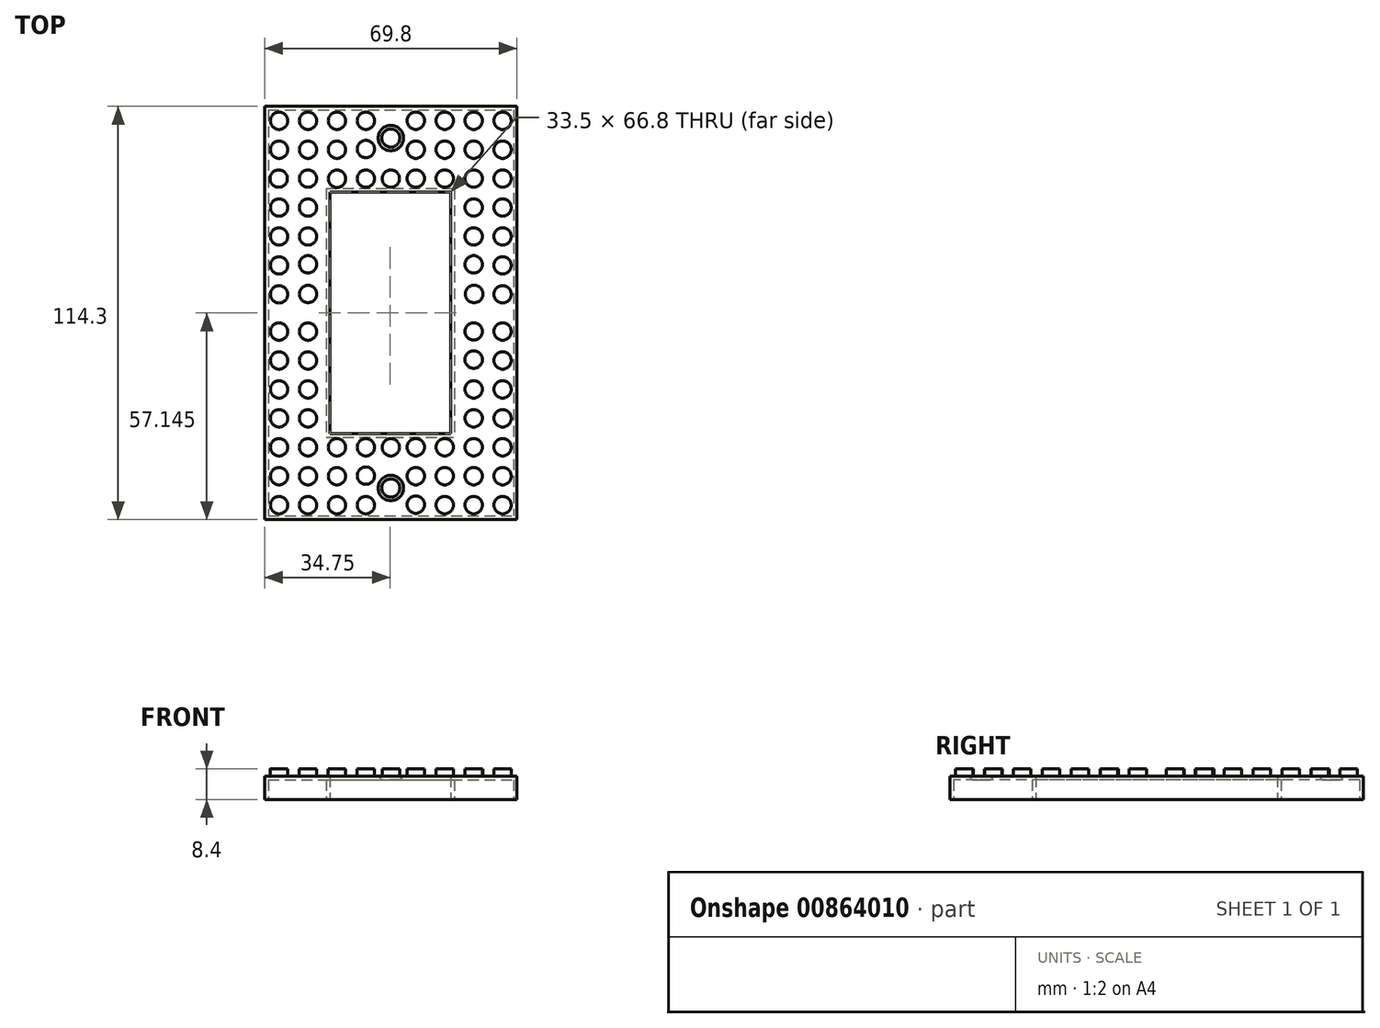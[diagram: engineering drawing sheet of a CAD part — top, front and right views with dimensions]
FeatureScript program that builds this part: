
annotation { "Feature Type Name" : "Feature", "Feature Type Description" : "" }
export const myFeature = defineFeature(function(context is Context, id is Id, definition is map)
    precondition{}
    {
        {
            var Q0;
            Q0=qCreatedBy(makeId("Top.planeOp"),FACE);
            var sketch = newSketch(context, id + "F0", { "sketchPlane" : qUnion([Q0])});
            skLineSegment(sketch, "E0.bottom", {"start": v(-34.9, 65.9) * mm, "end": v(34.9, 65.9) * mm});
            skLineSegment(sketch, "E0.top", {"start": v(-34.9, -48.4) * mm, "end": v(34.9, -48.4) * mm});
            skLineSegment(sketch, "E0.left", {"start": v(-34.9, 65.9) * mm, "end": v(-34.9, -48.4) * mm});
            skLineSegment(sketch, "E0.right", {"start": v(34.9, 65.9) * mm, "end": v(34.9, -48.4) * mm});
            skLineSegment(sketch, "E1.bottom", {"start": v(-16.9, 42.15) * mm, "end": v(16.6, 42.15) * mm});
            skLineSegment(sketch, "E1.top", {"start": v(-16.9, -24.65) * mm, "end": v(16.6, -24.65) * mm});
            skLineSegment(sketch, "E1.left", {"start": v(-16.9, 42.15) * mm, "end": v(-16.9, -24.65) * mm});
            skLineSegment(sketch, "E1.right", {"start": v(16.6, 42.15) * mm, "end": v(16.6, -24.65) * mm});
            skPoint(sketch, "E2", {"position": v(0, 57.15) * mm});
            skPoint(sketch, "E3", {"position": v(0, -39.65) * mm});
            skSolve(sketch);
        }
        {
            var Q0;
            Q0=makeQuery(id+"F0.imprint","IMPRINT",FACE,{"disambiguationData":[TD([[makeQuery(id+"F0.imprint","IMPRINT",EDGE,{"derivedFrom":sQuery(id+"F0.wireOp",EDGE,"E0.bottom")}),-1.0]])]});
            extrude(context, id + "F1", {"entities" : qUnion([Q0]), "depth" : 6.4 * mm, "offsetDistance" : 25 * mm});
        }
        {
            var Q0;
            Q0=makeQuery(id+"F1.opExtrude","CAP_FACE",FACE,{"disambiguationData":[OSD([sQuery(id+"F0.wireOp",EDGE,"E0.bottom"),sQuery(id+"F0.wireOp",EDGE,"E0.top"),sQuery(id+"F0.wireOp",EDGE,"E0.left"),sQuery(id+"F0.wireOp",EDGE,"E0.right"),sQuery(id+"F0.wireOp",EDGE,"E1.bottom"),sQuery(id+"F0.wireOp",EDGE,"E1.top"),sQuery(id+"F0.wireOp",EDGE,"E1.left"),sQuery(id+"F0.wireOp",EDGE,"E1.right"),sQuery(id+"F0.wireOp",EDGE,"O5FTPcTM-QUJB-rhsi-xSIB-Mxk94AfWPKoa"),sQuery(id+"F0.wireOp",EDGE,"3cRLo2FR-j5J2-G38M-Sb06-RW8L4j5h2IR9")])],"isStart":true});
            shell(context, id + "F2", {"entities" : qUnion([Q0]), "thickness" : 1 * mm});
        }
        {
            var Q0;
            Q0=makeQuery(id+"F1.opExtrude","CAP_FACE",FACE,{"disambiguationData":[OSD([sQuery(id+"F0.wireOp",EDGE,"E0.bottom"),sQuery(id+"F0.wireOp",EDGE,"E0.top"),sQuery(id+"F0.wireOp",EDGE,"E0.left"),sQuery(id+"F0.wireOp",EDGE,"E0.right"),sQuery(id+"F0.wireOp",EDGE,"E1.bottom"),sQuery(id+"F0.wireOp",EDGE,"E1.top"),sQuery(id+"F0.wireOp",EDGE,"E1.left"),sQuery(id+"F0.wireOp",EDGE,"E1.right"),sQuery(id+"F0.wireOp",EDGE,"O5FTPcTM-QUJB-rhsi-xSIB-Mxk94AfWPKoa"),sQuery(id+"F0.wireOp",EDGE,"3cRLo2FR-j5J2-G38M-Sb06-RW8L4j5h2IR9")])],"isStart":false});
            var sketch = newSketch(context, id + "F3", { "sketchPlane" : qUnion([Q0])});
            skLineSegment(sketch, "E4", {"start": v(-34.9, 65.9) * mm, "end": v(34.9, 65.9) * mm});
            skLineSegment(sketch, "E5", {"start": v(34.9, 65.9) * mm, "end": v(34.9, -48.4) * mm});
            skLineSegment(sketch, "E6", {"start": v(34.9, -48.4) * mm, "end": v(-34.9, -48.4) * mm});
            skLineSegment(sketch, "E7", {"start": v(-34.9, -48.4) * mm, "end": v(-34.9, 65.9) * mm});
            skCircle(sketch, "E8", {"center": v(-30.9, 61.9) * mm, "radius": 2.4 * mm});
            skCircle(sketch, "E9", {"center": v(-30.9, 53.9) * mm, "radius": 2.4 * mm});
            skCircle(sketch, "E10", {"center": v(-31, 45.9) * mm, "radius": 2.4 * mm});
            skCircle(sketch, "E11", {"center": v(-30.9, 37.9) * mm, "radius": 2.4 * mm});
            skCircle(sketch, "E12", {"center": v(-30.9, 29.9) * mm, "radius": 2.4 * mm});
            skCircle(sketch, "E13", {"center": v(-30.9, 21.9) * mm, "radius": 2.4 * mm});
            skCircle(sketch, "E14", {"center": v(-30.9, 13.9) * mm, "radius": 2.4 * mm});
            skCircle(sketch, "E15", {"center": v(-30.9, 3.6) * mm, "radius": 2.4 * mm});
            skCircle(sketch, "E16", {"center": v(-30.9, -4.4) * mm, "radius": 2.4 * mm});
            skCircle(sketch, "E17", {"center": v(-30.9, -12.4) * mm, "radius": 2.4 * mm});
            skCircle(sketch, "E18", {"center": v(-30.9, -20.4) * mm, "radius": 2.4 * mm});
            skCircle(sketch, "E19", {"center": v(-30.9, -28.4) * mm, "radius": 2.4 * mm});
            skCircle(sketch, "E20", {"center": v(-30.9, -36.4) * mm, "radius": 2.4 * mm});
            skCircle(sketch, "E21", {"center": v(-30.9, -44.4) * mm, "radius": 2.4 * mm});
            skCircle(sketch, "E22", {"center": v(-22.9, 61.9) * mm, "radius": 2.4 * mm});
            skCircle(sketch, "E23", {"center": v(-22.9, 53.9) * mm, "radius": 2.4 * mm});
            skCircle(sketch, "E24", {"center": v(-22.9, 37.9) * mm, "radius": 2.4 * mm});
            skCircle(sketch, "E25", {"center": v(-22.9, 29.9) * mm, "radius": 2.4 * mm});
            skCircle(sketch, "E26", {"center": v(-22.9, 22.22) * mm, "radius": 2.4 * mm});
            skCircle(sketch, "E27", {"center": v(-22.9, 13.98) * mm, "radius": 2.4 * mm});
            skCircle(sketch, "E28", {"center": v(-22.9, 3.6) * mm, "radius": 2.4 * mm});
            skCircle(sketch, "E29", {"center": v(-22.9, -4.4) * mm, "radius": 2.4 * mm});
            skCircle(sketch, "E30", {"center": v(-22.9, -12.4) * mm, "radius": 2.4 * mm});
            skCircle(sketch, "E31", {"center": v(-22.9, -20.4) * mm, "radius": 2.4 * mm});
            skCircle(sketch, "E32", {"center": v(-22.9, -28.4) * mm, "radius": 2.4 * mm});
            skCircle(sketch, "E33", {"center": v(-22.9, -36.4) * mm, "radius": 2.4 * mm});
            skCircle(sketch, "E34", {"center": v(-22.9, -44.4) * mm, "radius": 2.4 * mm});
            skCircle(sketch, "E35", {"center": v(-14.9, 61.9) * mm, "radius": 2.4 * mm});
            skCircle(sketch, "E36", {"center": v(-14.9, 53.9) * mm, "radius": 2.4 * mm});
            skCircle(sketch, "E37", {"center": v(-14.9, 45.86) * mm, "radius": 2.4 * mm});
            skCircle(sketch, "E38", {"center": v(-6.9, 61.9) * mm, "radius": 2.4 * mm});
            skCircle(sketch, "E39", {"center": v(-6.9, 54.09) * mm, "radius": 2.4 * mm});
            skCircle(sketch, "E40", {"center": v(-6.9, 45.9) * mm, "radius": 2.4 * mm});
            skCircle(sketch, "E41", {"center": v(-14.9, -28.4) * mm, "radius": 2.4 * mm});
            skCircle(sketch, "E42", {"center": v(-14.9, -36.4) * mm, "radius": 2.4 * mm});
            skCircle(sketch, "E43", {"center": v(-14.9, -44.4) * mm, "radius": 2.4 * mm});
            skCircle(sketch, "E44", {"center": v(0, 45.9) * mm, "radius": 2.4 * mm});
            skCircle(sketch, "E45", {"center": v(6.9, 61.9) * mm, "radius": 2.4 * mm});
            skCircle(sketch, "E46", {"center": v(6.9, 53.88) * mm, "radius": 2.4 * mm});
            skCircle(sketch, "E47", {"center": v(6.9, 45.9) * mm, "radius": 2.4 * mm});
            skCircle(sketch, "E48", {"center": v(14.9, 61.9) * mm, "radius": 2.4 * mm});
            skCircle(sketch, "E49", {"center": v(14.9, 53.9) * mm, "radius": 2.4 * mm});
            skCircle(sketch, "E50", {"center": v(14.9, 45.9) * mm, "radius": 2.4 * mm});
            skCircle(sketch, "E51", {"center": v(-6.9, -28.4) * mm, "radius": 2.4 * mm});
            skCircle(sketch, "E52", {"center": v(-6.9, -36.25) * mm, "radius": 2.4 * mm});
            skCircle(sketch, "E53", {"center": v(-6.9, -44.4) * mm, "radius": 2.4 * mm});
            skCircle(sketch, "E54", {"center": v(0, -28.4) * mm, "radius": 2.4 * mm});
            skCircle(sketch, "E55", {"center": v(6.9, -28.4) * mm, "radius": 2.4 * mm});
            skCircle(sketch, "E56", {"center": v(6.9, -36.4) * mm, "radius": 2.4 * mm});
            skCircle(sketch, "E57", {"center": v(6.9, -44.28) * mm, "radius": 2.4 * mm});
            skCircle(sketch, "E58", {"center": v(14.9, -28.4) * mm, "radius": 2.4 * mm});
            skCircle(sketch, "E59", {"center": v(14.9, -36.4) * mm, "radius": 2.4 * mm});
            skCircle(sketch, "E60", {"center": v(14.9, -44.4) * mm, "radius": 2.4 * mm});
            skCircle(sketch, "E61", {"center": v(22.9, 61.9) * mm, "radius": 2.4 * mm});
            skCircle(sketch, "E62", {"center": v(22.9, 53.9) * mm, "radius": 2.4 * mm});
            skCircle(sketch, "E63", {"center": v(22.9, 37.9) * mm, "radius": 2.4 * mm});
            skCircle(sketch, "E64", {"center": v(22.9, 29.9) * mm, "radius": 2.4 * mm});
            skCircle(sketch, "E65", {"center": v(22.9, 22.22) * mm, "radius": 2.4 * mm});
            skCircle(sketch, "E66", {"center": v(23.03, 13.98) * mm, "radius": 2.4 * mm});
            skCircle(sketch, "E67", {"center": v(22.9, 3.64) * mm, "radius": 2.4 * mm});
            skCircle(sketch, "E68", {"center": v(22.9, -4.17) * mm, "radius": 2.4 * mm});
            skCircle(sketch, "E69", {"center": v(22.9, -12.4) * mm, "radius": 2.4 * mm});
            skCircle(sketch, "E70", {"center": v(22.9, -20.4) * mm, "radius": 2.4 * mm});
            skCircle(sketch, "E71", {"center": v(22.9, -28.4) * mm, "radius": 2.4 * mm});
            skCircle(sketch, "E72", {"center": v(22.9, -36.4) * mm, "radius": 2.4 * mm});
            skCircle(sketch, "E73", {"center": v(22.9, -44.4) * mm, "radius": 2.4 * mm});
            skCircle(sketch, "E74", {"center": v(30.9, -44.4) * mm, "radius": 2.4 * mm});
            skCircle(sketch, "E75", {"center": v(30.9, -36.4) * mm, "radius": 2.4 * mm});
            skCircle(sketch, "E76", {"center": v(30.9, -28.4) * mm, "radius": 2.4 * mm});
            skCircle(sketch, "E77", {"center": v(30.9, -20.4) * mm, "radius": 2.4 * mm});
            skCircle(sketch, "E78", {"center": v(30.9, -12.4) * mm, "radius": 2.4 * mm});
            skCircle(sketch, "E79", {"center": v(30.9, -4.4) * mm, "radius": 2.4 * mm});
            skCircle(sketch, "E80", {"center": v(30.9, 3.6) * mm, "radius": 2.4 * mm});
            skCircle(sketch, "E81", {"center": v(30.9, 13.9) * mm, "radius": 2.4 * mm});
            skCircle(sketch, "E82", {"center": v(30.9, 21.9) * mm, "radius": 2.4 * mm});
            skCircle(sketch, "E83", {"center": v(30.9, 29.9) * mm, "radius": 2.4 * mm});
            skCircle(sketch, "E84", {"center": v(30.9, 37.9) * mm, "radius": 2.4 * mm});
            skCircle(sketch, "E85", {"center": v(30.9, 45.9) * mm, "radius": 2.4 * mm});
            skCircle(sketch, "E86", {"center": v(30.9, 53.9) * mm, "radius": 2.4 * mm});
            skCircle(sketch, "E87", {"center": v(30.9, 61.9) * mm, "radius": 2.4 * mm});
            skCircle(sketch, "E88", {"center": v(-22.9, 45.9) * mm, "radius": 2.4 * mm});
            skCircle(sketch, "E89", {"center": v(22.9, 45.9) * mm, "radius": 2.4 * mm});
            skPoint(sketch, "E90", {"position": v(0, 57.12) * mm});
            skPoint(sketch, "E90.positionSnap0", {"position": v(0, 65.9) * mm});
            skPoint(sketch, "E91", {"position": v(0, -39.67) * mm});
            skSolve(sketch);
        }
        {
            var Q0;
            Q0=makeQuery(id+"F3.imprint","IMPRINT",FACE,{"disambiguationData":[TD([[makeQuery(id+"F3.imprint","IMPRINT",EDGE,{"derivedFrom":sQuery(id+"F3.wireOp",EDGE,"E74")}),1.0]])]});
            var Q1;
            Q1=makeQuery(id+"F3.imprint","IMPRINT",FACE,{"disambiguationData":[TD([[makeQuery(id+"F3.imprint","IMPRINT",EDGE,{"derivedFrom":sQuery(id+"F3.wireOp",EDGE,"E73")}),1.0]])]});
            var Q2;
            Q2=makeQuery(id+"F3.imprint","IMPRINT",FACE,{"disambiguationData":[TD([[makeQuery(id+"F3.imprint","IMPRINT",EDGE,{"derivedFrom":sQuery(id+"F3.wireOp",EDGE,"E60")}),1.0]])]});
            var Q3;
            Q3=makeQuery(id+"F3.imprint","IMPRINT",FACE,{"disambiguationData":[TD([[makeQuery(id+"F3.imprint","IMPRINT",EDGE,{"derivedFrom":sQuery(id+"F3.wireOp",EDGE,"E57")}),1.0]])]});
            var Q4;
            Q4=makeQuery(id+"F3.imprint","IMPRINT",FACE,{"disambiguationData":[TD([[makeQuery(id+"F3.imprint","IMPRINT",EDGE,{"derivedFrom":sQuery(id+"F3.wireOp",EDGE,"E53")}),1.0]])]});
            var Q5;
            Q5=makeQuery(id+"F3.imprint","IMPRINT",FACE,{"disambiguationData":[TD([[makeQuery(id+"F3.imprint","IMPRINT",EDGE,{"derivedFrom":sQuery(id+"F3.wireOp",EDGE,"E43")}),1.0]])]});
            var Q6;
            Q6=makeQuery(id+"F3.imprint","IMPRINT",FACE,{"disambiguationData":[TD([[makeQuery(id+"F3.imprint","IMPRINT",EDGE,{"derivedFrom":sQuery(id+"F3.wireOp",EDGE,"E34")}),1.0]])]});
            var Q7;
            Q7=makeQuery(id+"F3.imprint","IMPRINT",FACE,{"disambiguationData":[TD([[makeQuery(id+"F3.imprint","IMPRINT",EDGE,{"derivedFrom":sQuery(id+"F3.wireOp",EDGE,"E21")}),1.0]])]});
            var Q8;
            Q8=makeQuery(id+"F3.imprint","IMPRINT",FACE,{"disambiguationData":[TD([[makeQuery(id+"F3.imprint","IMPRINT",EDGE,{"derivedFrom":sQuery(id+"F3.wireOp",EDGE,"E20")}),1.0]])]});
            var Q9;
            Q9=makeQuery(id+"F3.imprint","IMPRINT",FACE,{"disambiguationData":[TD([[makeQuery(id+"F3.imprint","IMPRINT",EDGE,{"derivedFrom":sQuery(id+"F3.wireOp",EDGE,"E33")}),1.0]])]});
            var Q10;
            Q10=makeQuery(id+"F3.imprint","IMPRINT",FACE,{"disambiguationData":[TD([[makeQuery(id+"F3.imprint","IMPRINT",EDGE,{"derivedFrom":sQuery(id+"F3.wireOp",EDGE,"E42")}),1.0]])]});
            var Q11;
            Q11=makeQuery(id+"F3.imprint","IMPRINT",FACE,{"disambiguationData":[TD([[makeQuery(id+"F3.imprint","IMPRINT",EDGE,{"derivedFrom":sQuery(id+"F3.wireOp",EDGE,"E52")}),1.0]])]});
            var Q12;
            Q12=makeQuery(id+"F3.imprint","IMPRINT",FACE,{"disambiguationData":[TD([[makeQuery(id+"F3.imprint","IMPRINT",EDGE,{"derivedFrom":sQuery(id+"F3.wireOp",EDGE,"E56")}),1.0]])]});
            var Q13;
            Q13=makeQuery(id+"F3.imprint","IMPRINT",FACE,{"disambiguationData":[TD([[makeQuery(id+"F3.imprint","IMPRINT",EDGE,{"derivedFrom":sQuery(id+"F3.wireOp",EDGE,"E59")}),1.0]])]});
            var Q14;
            Q14=makeQuery(id+"F3.imprint","IMPRINT",FACE,{"disambiguationData":[TD([[makeQuery(id+"F3.imprint","IMPRINT",EDGE,{"derivedFrom":sQuery(id+"F3.wireOp",EDGE,"E72")}),1.0]])]});
            var Q15;
            Q15=makeQuery(id+"F3.imprint","IMPRINT",FACE,{"disambiguationData":[TD([[makeQuery(id+"F3.imprint","IMPRINT",EDGE,{"derivedFrom":sQuery(id+"F3.wireOp",EDGE,"E75")}),1.0]])]});
            var Q16;
            Q16=makeQuery(id+"F3.imprint","IMPRINT",FACE,{"disambiguationData":[TD([[makeQuery(id+"F3.imprint","IMPRINT",EDGE,{"derivedFrom":sQuery(id+"F3.wireOp",EDGE,"E76")}),1.0]])]});
            var Q17;
            Q17=makeQuery(id+"F3.imprint","IMPRINT",FACE,{"disambiguationData":[TD([[makeQuery(id+"F3.imprint","IMPRINT",EDGE,{"derivedFrom":sQuery(id+"F3.wireOp",EDGE,"E71")}),1.0]])]});
            var Q18;
            Q18=makeQuery(id+"F3.imprint","IMPRINT",FACE,{"disambiguationData":[TD([[makeQuery(id+"F3.imprint","IMPRINT",EDGE,{"derivedFrom":sQuery(id+"F3.wireOp",EDGE,"E58")}),1.0]])]});
            var Q19;
            Q19=makeQuery(id+"F3.imprint","IMPRINT",FACE,{"disambiguationData":[TD([[makeQuery(id+"F3.imprint","IMPRINT",EDGE,{"derivedFrom":sQuery(id+"F3.wireOp",EDGE,"E55")}),1.0]])]});
            var Q20;
            Q20=makeQuery(id+"F3.imprint","IMPRINT",FACE,{"disambiguationData":[TD([[makeQuery(id+"F3.imprint","IMPRINT",EDGE,{"derivedFrom":sQuery(id+"F3.wireOp",EDGE,"E54")}),1.0]])]});
            var Q21;
            Q21=makeQuery(id+"F3.imprint","IMPRINT",FACE,{"disambiguationData":[TD([[makeQuery(id+"F3.imprint","IMPRINT",EDGE,{"derivedFrom":sQuery(id+"F3.wireOp",EDGE,"E51")}),1.0]])]});
            var Q22;
            Q22=makeQuery(id+"F3.imprint","IMPRINT",FACE,{"disambiguationData":[TD([[makeQuery(id+"F3.imprint","IMPRINT",EDGE,{"derivedFrom":sQuery(id+"F3.wireOp",EDGE,"E41")}),1.0]])]});
            var Q23;
            Q23=makeQuery(id+"F3.imprint","IMPRINT",FACE,{"disambiguationData":[TD([[makeQuery(id+"F3.imprint","IMPRINT",EDGE,{"derivedFrom":sQuery(id+"F3.wireOp",EDGE,"E32")}),1.0]])]});
            var Q24;
            Q24=makeQuery(id+"F3.imprint","IMPRINT",FACE,{"disambiguationData":[TD([[makeQuery(id+"F3.imprint","IMPRINT",EDGE,{"derivedFrom":sQuery(id+"F3.wireOp",EDGE,"E19")}),1.0]])]});
            var Q25;
            Q25=makeQuery(id+"F3.imprint","IMPRINT",FACE,{"disambiguationData":[TD([[makeQuery(id+"F3.imprint","IMPRINT",EDGE,{"derivedFrom":sQuery(id+"F3.wireOp",EDGE,"E18")}),1.0]])]});
            var Q26;
            Q26=makeQuery(id+"F3.imprint","IMPRINT",FACE,{"disambiguationData":[TD([[makeQuery(id+"F3.imprint","IMPRINT",EDGE,{"derivedFrom":sQuery(id+"F3.wireOp",EDGE,"E31")}),1.0]])]});
            var Q27;
            Q27=makeQuery(id+"F3.imprint","IMPRINT",FACE,{"disambiguationData":[TD([[makeQuery(id+"F3.imprint","IMPRINT",EDGE,{"derivedFrom":sQuery(id+"F3.wireOp",EDGE,"E70")}),1.0]])]});
            var Q28;
            Q28=makeQuery(id+"F3.imprint","IMPRINT",FACE,{"disambiguationData":[TD([[makeQuery(id+"F3.imprint","IMPRINT",EDGE,{"derivedFrom":sQuery(id+"F3.wireOp",EDGE,"E77")}),1.0]])]});
            var Q29;
            Q29=makeQuery(id+"F3.imprint","IMPRINT",FACE,{"disambiguationData":[TD([[makeQuery(id+"F3.imprint","IMPRINT",EDGE,{"derivedFrom":sQuery(id+"F3.wireOp",EDGE,"E17")}),1.0]])]});
            var Q30;
            Q30=makeQuery(id+"F3.imprint","IMPRINT",FACE,{"disambiguationData":[TD([[makeQuery(id+"F3.imprint","IMPRINT",EDGE,{"derivedFrom":sQuery(id+"F3.wireOp",EDGE,"E16")}),1.0]])]});
            var Q31;
            Q31=makeQuery(id+"F3.imprint","IMPRINT",FACE,{"disambiguationData":[TD([[makeQuery(id+"F3.imprint","IMPRINT",EDGE,{"derivedFrom":sQuery(id+"F3.wireOp",EDGE,"E15")}),1.0]])]});
            var Q32;
            Q32=makeQuery(id+"F3.imprint","IMPRINT",FACE,{"disambiguationData":[TD([[makeQuery(id+"F3.imprint","IMPRINT",EDGE,{"derivedFrom":sQuery(id+"F3.wireOp",EDGE,"E14")}),1.0]])]});
            var Q33;
            Q33=makeQuery(id+"F3.imprint","IMPRINT",FACE,{"disambiguationData":[TD([[makeQuery(id+"F3.imprint","IMPRINT",EDGE,{"derivedFrom":sQuery(id+"F3.wireOp",EDGE,"E12")}),1.0]])]});
            var Q34;
            Q34=makeQuery(id+"F3.imprint","IMPRINT",FACE,{"disambiguationData":[TD([[makeQuery(id+"F3.imprint","IMPRINT",EDGE,{"derivedFrom":sQuery(id+"F3.wireOp",EDGE,"E13")}),1.0]])]});
            var Q35;
            Q35=makeQuery(id+"F3.imprint","IMPRINT",FACE,{"disambiguationData":[TD([[makeQuery(id+"F3.imprint","IMPRINT",EDGE,{"derivedFrom":sQuery(id+"F3.wireOp",EDGE,"E11")}),1.0]])]});
            var Q36;
            Q36=makeQuery(id+"F3.imprint","IMPRINT",FACE,{"disambiguationData":[TD([[makeQuery(id+"F3.imprint","IMPRINT",EDGE,{"derivedFrom":sQuery(id+"F3.wireOp",EDGE,"E24")}),1.0]])]});
            var Q37;
            Q37=makeQuery(id+"F3.imprint","IMPRINT",FACE,{"disambiguationData":[TD([[makeQuery(id+"F3.imprint","IMPRINT",EDGE,{"derivedFrom":sQuery(id+"F3.wireOp",EDGE,"E25")}),1.0]])]});
            var Q38;
            Q38=makeQuery(id+"F3.imprint","IMPRINT",FACE,{"disambiguationData":[TD([[makeQuery(id+"F3.imprint","IMPRINT",EDGE,{"derivedFrom":sQuery(id+"F3.wireOp",EDGE,"E26")}),1.0]])]});
            var Q39;
            Q39=makeQuery(id+"F3.imprint","IMPRINT",FACE,{"disambiguationData":[TD([[makeQuery(id+"F3.imprint","IMPRINT",EDGE,{"derivedFrom":sQuery(id+"F3.wireOp",EDGE,"E27")}),1.0]])]});
            var Q40;
            Q40=makeQuery(id+"F3.imprint","IMPRINT",FACE,{"disambiguationData":[TD([[makeQuery(id+"F3.imprint","IMPRINT",EDGE,{"derivedFrom":sQuery(id+"F3.wireOp",EDGE,"E28")}),1.0]])]});
            var Q41;
            Q41=makeQuery(id+"F3.imprint","IMPRINT",FACE,{"disambiguationData":[TD([[makeQuery(id+"F3.imprint","IMPRINT",EDGE,{"derivedFrom":sQuery(id+"F3.wireOp",EDGE,"E29")}),1.0]])]});
            var Q42;
            Q42=makeQuery(id+"F3.imprint","IMPRINT",FACE,{"disambiguationData":[TD([[makeQuery(id+"F3.imprint","IMPRINT",EDGE,{"derivedFrom":sQuery(id+"F3.wireOp",EDGE,"E30")}),1.0]])]});
            var Q43;
            Q43=makeQuery(id+"F3.imprint","IMPRINT",FACE,{"disambiguationData":[TD([[makeQuery(id+"F3.imprint","IMPRINT",EDGE,{"derivedFrom":sQuery(id+"F3.wireOp",EDGE,"E69")}),1.0]])]});
            var Q44;
            Q44=makeQuery(id+"F3.imprint","IMPRINT",FACE,{"disambiguationData":[TD([[makeQuery(id+"F3.imprint","IMPRINT",EDGE,{"derivedFrom":sQuery(id+"F3.wireOp",EDGE,"E68")}),1.0]])]});
            var Q45;
            Q45=makeQuery(id+"F3.imprint","IMPRINT",FACE,{"disambiguationData":[TD([[makeQuery(id+"F3.imprint","IMPRINT",EDGE,{"derivedFrom":sQuery(id+"F3.wireOp",EDGE,"E67")}),1.0]])]});
            var Q46;
            Q46=makeQuery(id+"F3.imprint","IMPRINT",FACE,{"disambiguationData":[TD([[makeQuery(id+"F3.imprint","IMPRINT",EDGE,{"derivedFrom":sQuery(id+"F3.wireOp",EDGE,"E66")}),1.0]])]});
            var Q47;
            Q47=makeQuery(id+"F3.imprint","IMPRINT",FACE,{"disambiguationData":[TD([[makeQuery(id+"F3.imprint","IMPRINT",EDGE,{"derivedFrom":sQuery(id+"F3.wireOp",EDGE,"E65")}),1.0]])]});
            var Q48;
            Q48=makeQuery(id+"F3.imprint","IMPRINT",FACE,{"disambiguationData":[TD([[makeQuery(id+"F3.imprint","IMPRINT",EDGE,{"derivedFrom":sQuery(id+"F3.wireOp",EDGE,"E64")}),1.0]])]});
            var Q49;
            Q49=makeQuery(id+"F3.imprint","IMPRINT",FACE,{"disambiguationData":[TD([[makeQuery(id+"F3.imprint","IMPRINT",EDGE,{"derivedFrom":sQuery(id+"F3.wireOp",EDGE,"E63")}),1.0]])]});
            var Q50;
            Q50=makeQuery(id+"F3.imprint","IMPRINT",FACE,{"disambiguationData":[TD([[makeQuery(id+"F3.imprint","IMPRINT",EDGE,{"derivedFrom":sQuery(id+"F3.wireOp",EDGE,"E84")}),1.0]])]});
            var Q51;
            Q51=makeQuery(id+"F3.imprint","IMPRINT",FACE,{"disambiguationData":[TD([[makeQuery(id+"F3.imprint","IMPRINT",EDGE,{"derivedFrom":sQuery(id+"F3.wireOp",EDGE,"E83")}),1.0]])]});
            var Q52;
            Q52=makeQuery(id+"F3.imprint","IMPRINT",FACE,{"disambiguationData":[TD([[makeQuery(id+"F3.imprint","IMPRINT",EDGE,{"derivedFrom":sQuery(id+"F3.wireOp",EDGE,"E82")}),1.0]])]});
            var Q53;
            Q53=makeQuery(id+"F3.imprint","IMPRINT",FACE,{"disambiguationData":[TD([[makeQuery(id+"F3.imprint","IMPRINT",EDGE,{"derivedFrom":sQuery(id+"F3.wireOp",EDGE,"E81")}),1.0]])]});
            var Q54;
            Q54=makeQuery(id+"F3.imprint","IMPRINT",FACE,{"disambiguationData":[TD([[makeQuery(id+"F3.imprint","IMPRINT",EDGE,{"derivedFrom":sQuery(id+"F3.wireOp",EDGE,"E80")}),1.0]])]});
            var Q55;
            Q55=makeQuery(id+"F3.imprint","IMPRINT",FACE,{"disambiguationData":[TD([[makeQuery(id+"F3.imprint","IMPRINT",EDGE,{"derivedFrom":sQuery(id+"F3.wireOp",EDGE,"E79")}),1.0]])]});
            var Q56;
            Q56=makeQuery(id+"F3.imprint","IMPRINT",FACE,{"disambiguationData":[TD([[makeQuery(id+"F3.imprint","IMPRINT",EDGE,{"derivedFrom":sQuery(id+"F3.wireOp",EDGE,"E78")}),1.0]])]});
            var Q57;
            Q57=makeQuery(id+"F3.imprint","IMPRINT",FACE,{"disambiguationData":[TD([[makeQuery(id+"F3.imprint","IMPRINT",EDGE,{"derivedFrom":sQuery(id+"F3.wireOp",EDGE,"E8")}),1.0]])]});
            var Q58;
            Q58=makeQuery(id+"F3.imprint","IMPRINT",FACE,{"disambiguationData":[TD([[makeQuery(id+"F3.imprint","IMPRINT",EDGE,{"derivedFrom":sQuery(id+"F3.wireOp",EDGE,"E9")}),1.0]])]});
            var Q59;
            Q59=makeQuery(id+"F3.imprint","IMPRINT",FACE,{"disambiguationData":[TD([[makeQuery(id+"F3.imprint","IMPRINT",EDGE,{"derivedFrom":sQuery(id+"F3.wireOp",EDGE,"E10")}),1.0]])]});
            var Q60;
            Q60=makeQuery(id+"F3.imprint","IMPRINT",FACE,{"disambiguationData":[TD([[makeQuery(id+"F3.imprint","IMPRINT",EDGE,{"derivedFrom":sQuery(id+"F3.wireOp",EDGE,"E88")}),1.0]])]});
            var Q61;
            Q61=makeQuery(id+"F3.imprint","IMPRINT",FACE,{"disambiguationData":[TD([[makeQuery(id+"F3.imprint","IMPRINT",EDGE,{"derivedFrom":sQuery(id+"F3.wireOp",EDGE,"E23")}),1.0]])]});
            var Q62;
            Q62=makeQuery(id+"F3.imprint","IMPRINT",FACE,{"disambiguationData":[TD([[makeQuery(id+"F3.imprint","IMPRINT",EDGE,{"derivedFrom":sQuery(id+"F3.wireOp",EDGE,"E22")}),1.0]])]});
            var Q63;
            Q63=makeQuery(id+"F3.imprint","IMPRINT",FACE,{"disambiguationData":[TD([[makeQuery(id+"F3.imprint","IMPRINT",EDGE,{"derivedFrom":sQuery(id+"F3.wireOp",EDGE,"E35")}),1.0]])]});
            var Q64;
            Q64=makeQuery(id+"F3.imprint","IMPRINT",FACE,{"disambiguationData":[TD([[makeQuery(id+"F3.imprint","IMPRINT",EDGE,{"derivedFrom":sQuery(id+"F3.wireOp",EDGE,"E36")}),1.0]])]});
            var Q65;
            Q65=makeQuery(id+"F3.imprint","IMPRINT",FACE,{"disambiguationData":[TD([[makeQuery(id+"F3.imprint","IMPRINT",EDGE,{"derivedFrom":sQuery(id+"F3.wireOp",EDGE,"E37")}),1.0]])]});
            var Q66;
            Q66=makeQuery(id+"F3.imprint","IMPRINT",FACE,{"disambiguationData":[TD([[makeQuery(id+"F3.imprint","IMPRINT",EDGE,{"derivedFrom":sQuery(id+"F3.wireOp",EDGE,"E40")}),1.0]])]});
            var Q67;
            Q67=makeQuery(id+"F3.imprint","IMPRINT",FACE,{"disambiguationData":[TD([[makeQuery(id+"F3.imprint","IMPRINT",EDGE,{"derivedFrom":sQuery(id+"F3.wireOp",EDGE,"E39")}),1.0]])]});
            var Q68;
            Q68=makeQuery(id+"F3.imprint","IMPRINT",FACE,{"disambiguationData":[TD([[makeQuery(id+"F3.imprint","IMPRINT",EDGE,{"derivedFrom":sQuery(id+"F3.wireOp",EDGE,"E38")}),1.0]])]});
            var Q69;
            Q69=makeQuery(id+"F3.imprint","IMPRINT",FACE,{"disambiguationData":[TD([[makeQuery(id+"F3.imprint","IMPRINT",EDGE,{"derivedFrom":sQuery(id+"F3.wireOp",EDGE,"E45")}),1.0]])]});
            var Q70;
            Q70=makeQuery(id+"F3.imprint","IMPRINT",FACE,{"disambiguationData":[TD([[makeQuery(id+"F3.imprint","IMPRINT",EDGE,{"derivedFrom":sQuery(id+"F3.wireOp",EDGE,"E44")}),1.0]])]});
            var Q71;
            Q71=makeQuery(id+"F3.imprint","IMPRINT",FACE,{"disambiguationData":[TD([[makeQuery(id+"F3.imprint","IMPRINT",EDGE,{"derivedFrom":sQuery(id+"F3.wireOp",EDGE,"E47")}),1.0]])]});
            var Q72;
            Q72=makeQuery(id+"F3.imprint","IMPRINT",FACE,{"disambiguationData":[TD([[makeQuery(id+"F3.imprint","IMPRINT",EDGE,{"derivedFrom":sQuery(id+"F3.wireOp",EDGE,"E46")}),1.0]])]});
            var Q73;
            Q73=makeQuery(id+"F3.imprint","IMPRINT",FACE,{"disambiguationData":[TD([[makeQuery(id+"F3.imprint","IMPRINT",EDGE,{"derivedFrom":sQuery(id+"F3.wireOp",EDGE,"E48")}),1.0]])]});
            var Q74;
            Q74=makeQuery(id+"F3.imprint","IMPRINT",FACE,{"disambiguationData":[TD([[makeQuery(id+"F3.imprint","IMPRINT",EDGE,{"derivedFrom":sQuery(id+"F3.wireOp",EDGE,"E49")}),1.0]])]});
            var Q75;
            Q75=makeQuery(id+"F3.imprint","IMPRINT",FACE,{"disambiguationData":[TD([[makeQuery(id+"F3.imprint","IMPRINT",EDGE,{"derivedFrom":sQuery(id+"F3.wireOp",EDGE,"E50")}),1.0]])]});
            var Q76;
            Q76=makeQuery(id+"F3.imprint","IMPRINT",FACE,{"disambiguationData":[TD([[makeQuery(id+"F3.imprint","IMPRINT",EDGE,{"derivedFrom":sQuery(id+"F3.wireOp",EDGE,"6TbLl8W2-29nf-ELlc-eapF-qSP463xOVyOk")}),1.0]])]});
            var Q77;
            Q77=makeQuery(id+"F3.imprint","IMPRINT",FACE,{"disambiguationData":[TD([[makeQuery(id+"F3.imprint","IMPRINT",EDGE,{"derivedFrom":sQuery(id+"F3.wireOp",EDGE,"E62")}),1.0]])]});
            var Q78;
            Q78=makeQuery(id+"F3.imprint","IMPRINT",FACE,{"disambiguationData":[TD([[makeQuery(id+"F3.imprint","IMPRINT",EDGE,{"derivedFrom":sQuery(id+"F3.wireOp",EDGE,"E61")}),1.0]])]});
            var Q79;
            Q79=makeQuery(id+"F3.imprint","IMPRINT",FACE,{"disambiguationData":[TD([[makeQuery(id+"F3.imprint","IMPRINT",EDGE,{"derivedFrom":sQuery(id+"F3.wireOp",EDGE,"E87")}),1.0]])]});
            var Q80;
            Q80=makeQuery(id+"F3.imprint","IMPRINT",FACE,{"disambiguationData":[TD([[makeQuery(id+"F3.imprint","IMPRINT",EDGE,{"derivedFrom":sQuery(id+"F3.wireOp",EDGE,"E86")}),1.0]])]});
            var Q81;
            Q81=makeQuery(id+"F3.imprint","IMPRINT",FACE,{"disambiguationData":[TD([[makeQuery(id+"F3.imprint","IMPRINT",EDGE,{"derivedFrom":sQuery(id+"F3.wireOp",EDGE,"E85")}),1.0]])]});
            extrude(context, id + "F4", {"entities" : qUnion([Q0, Q1, Q2, Q3, Q4, Q5, Q6, Q7, Q8, Q9, Q10, Q11, Q12, Q13, Q14, Q15, Q16, Q17, Q18, Q19, Q20, Q21, Q22, Q23, Q24, Q25, Q26, Q27, Q28, Q29, Q30, Q31, Q32, Q33, Q34, Q35, Q36, Q37, Q38, Q39, Q40, Q41, Q42, Q43, Q44, Q45, Q46, Q47, Q48, Q49, Q50, Q51, Q52, Q53, Q54, Q55, Q56, Q57, Q58, Q59, Q60, Q61, Q62, Q63, Q64, Q65, Q66, Q67, Q68, Q69, Q70, Q71, Q72, Q73, Q74, Q75, Q76, Q77, Q78, Q79, Q80, Q81]), "operationType" : NewBodyOperationType.ADD, "depth" : 2 * mm, "offsetDistance" : 25 * mm});
        }
        {
            var Q0;
            Q0=makeQuery(id+"F3.imprint","IMPRINT",FACE,{"disambiguationData":[TD([[makeQuery(id+"F3.imprint","IMPRINT",EDGE,{"derivedFrom":sQuery(id+"F3.wireOp",EDGE,"E89")}),1.0]])]});
            extrude(context, id + "F5", {"entities" : qUnion([Q0]), "operationType" : NewBodyOperationType.ADD, "depth" : 2 * mm, "offsetDistance" : 25 * mm});
        }
        {
            var Q0;
            Q0=sQuery(id+"F3.wireOp",VERTEX,"E90");
            var Q1;
            Q1=makeQuery(id+"F1.opExtrude","SWEPT_BODY",BODY,{"disambiguationData":[OSD([sQuery(id+"F0.wireOp",EDGE,"E0.bottom"),sQuery(id+"F0.wireOp",EDGE,"E0.top"),sQuery(id+"F0.wireOp",EDGE,"E0.left"),sQuery(id+"F0.wireOp",EDGE,"E0.right"),sQuery(id+"F0.wireOp",EDGE,"E1.bottom"),sQuery(id+"F0.wireOp",EDGE,"E1.top"),sQuery(id+"F0.wireOp",EDGE,"E1.left"),sQuery(id+"F0.wireOp",EDGE,"E1.right")])]});
            hole(context, id + "F6", {"style" : HoleStyle.C_SINK, "endStyle" : HoleEndStyle.THROUGH, "holeDiameter" : 4 * mm, "cSinkDiameter" : 7 * mm, "cSinkAngle" : 90 * degree, "majorDiameter" : 5 * mm, "isTappedThrough" : true, "tappedDepth" : 12 * mm, "tapClearance" : 3, "locations" : qUnion([Q0]), "scope" : qUnion([Q1])});
        }
        {
            var Q0;
            Q0=sQuery(id+"F3.wireOp",VERTEX,"E91");
            var Q1;
            Q1=makeQuery(id+"F1.opExtrude","SWEPT_BODY",BODY,{"disambiguationData":[OSD([sQuery(id+"F0.wireOp",EDGE,"E0.bottom"),sQuery(id+"F0.wireOp",EDGE,"E0.top"),sQuery(id+"F0.wireOp",EDGE,"E0.left"),sQuery(id+"F0.wireOp",EDGE,"E0.right"),sQuery(id+"F0.wireOp",EDGE,"E1.bottom"),sQuery(id+"F0.wireOp",EDGE,"E1.top"),sQuery(id+"F0.wireOp",EDGE,"E1.left"),sQuery(id+"F0.wireOp",EDGE,"E1.right")])]});
            hole(context, id + "F7", {"style" : HoleStyle.C_SINK, "endStyle" : HoleEndStyle.THROUGH, "holeDiameter" : 4 * mm, "cSinkDiameter" : 7 * mm, "cSinkAngle" : 90 * degree, "majorDiameter" : 5 * mm, "isTappedThrough" : true, "tappedDepth" : 12 * mm, "tapClearance" : 3, "locations" : qUnion([Q0]), "scope" : qUnion([Q1])});
        }
    });
